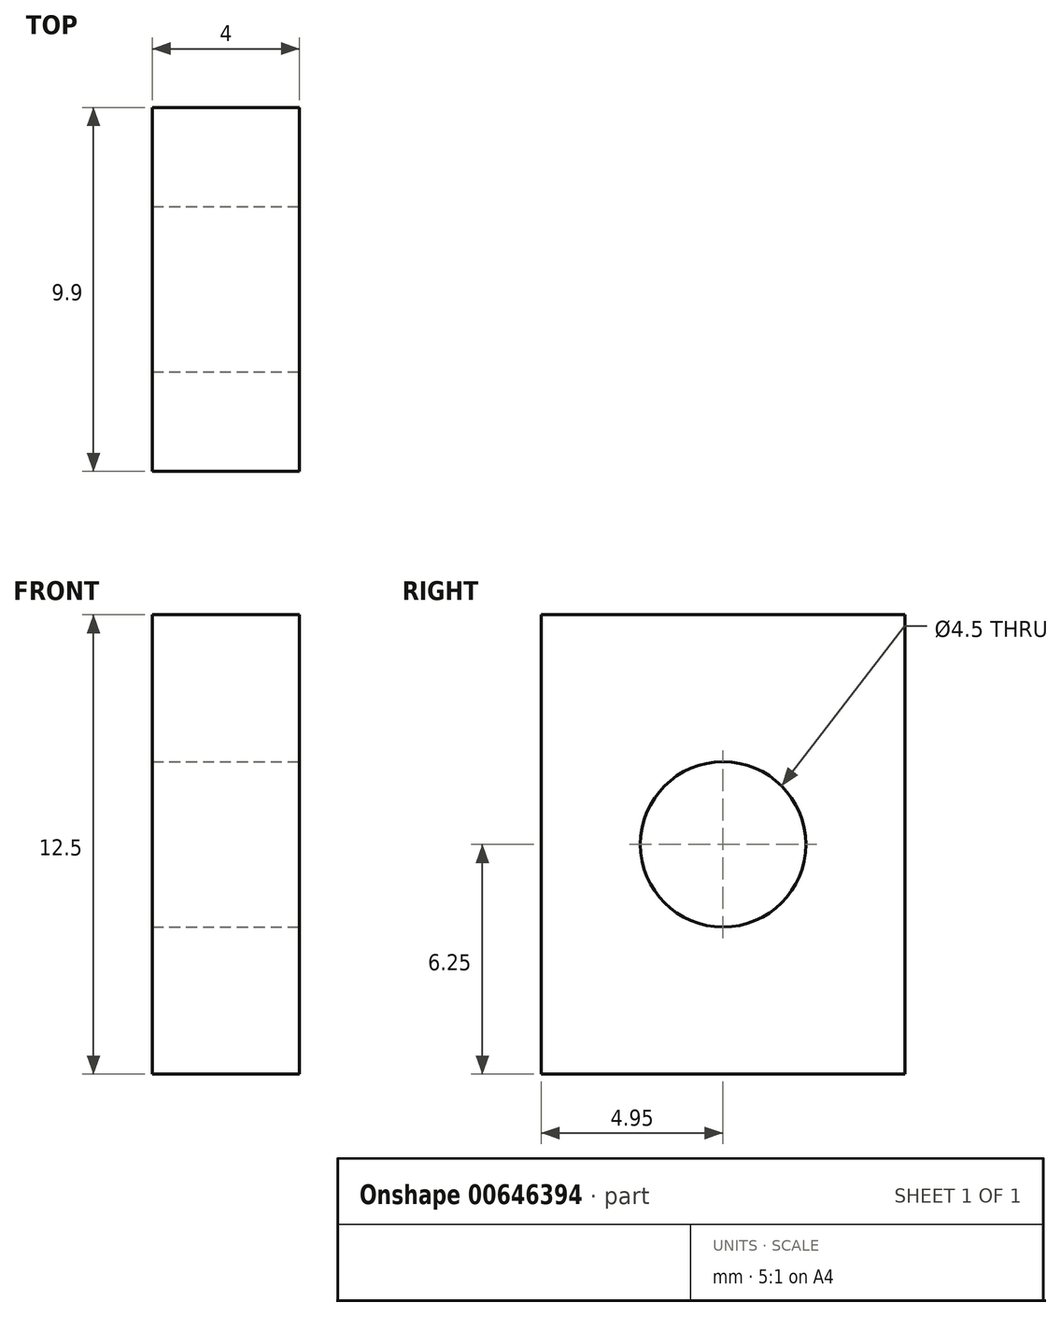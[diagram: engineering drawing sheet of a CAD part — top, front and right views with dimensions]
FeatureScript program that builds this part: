
annotation { "Feature Type Name" : "Feature", "Feature Type Description" : "" }
export const myFeature = defineFeature(function(context is Context, id is Id, definition is map)
    precondition{}
    {
        {
            var Q0;
            Q0=qCreatedBy(makeId("Right.planeOp"),FACE);
            var sketch = newSketch(context, id + "F0", { "sketchPlane" : qUnion([Q0])});
            skLineSegment(sketch, "E0.bottom", {"start": v(4.95, 6.25) * mm, "end": v(-4.95, 6.25) * mm});
            skLineSegment(sketch, "E0.top", {"start": v(4.95, -6.25) * mm, "end": v(-4.95, -6.25) * mm});
            skLineSegment(sketch, "E0.left", {"start": v(4.95, 6.25) * mm, "end": v(4.95, -6.25) * mm});
            skLineSegment(sketch, "E0.right", {"start": v(-4.95, 6.25) * mm, "end": v(-4.95, -6.25) * mm});
            skPoint(sketch, "E0.middle", {"position": v(0, 0) * mm});
            skCircle(sketch, "E1", {"center": v(0, 0) * mm, "radius": 2.25 * mm});
            skSolve(sketch);
        }
        {
            var Q0;
            Q0=makeQuery(id+"F0.imprint","IMPRINT",FACE,{"disambiguationData":[TD([[makeQuery(id+"F0.imprint","IMPRINT",EDGE,{"derivedFrom":sQuery(id+"F0.wireOp",EDGE,"E0.bottom")}),1.0]])]});
            extrude(context, id + "F1", {"entities" : qUnion([Q0]), "oppositeDirection" : true, "depth" : 4 * mm, "offsetDistance" : 25 * mm});
        }
    });
